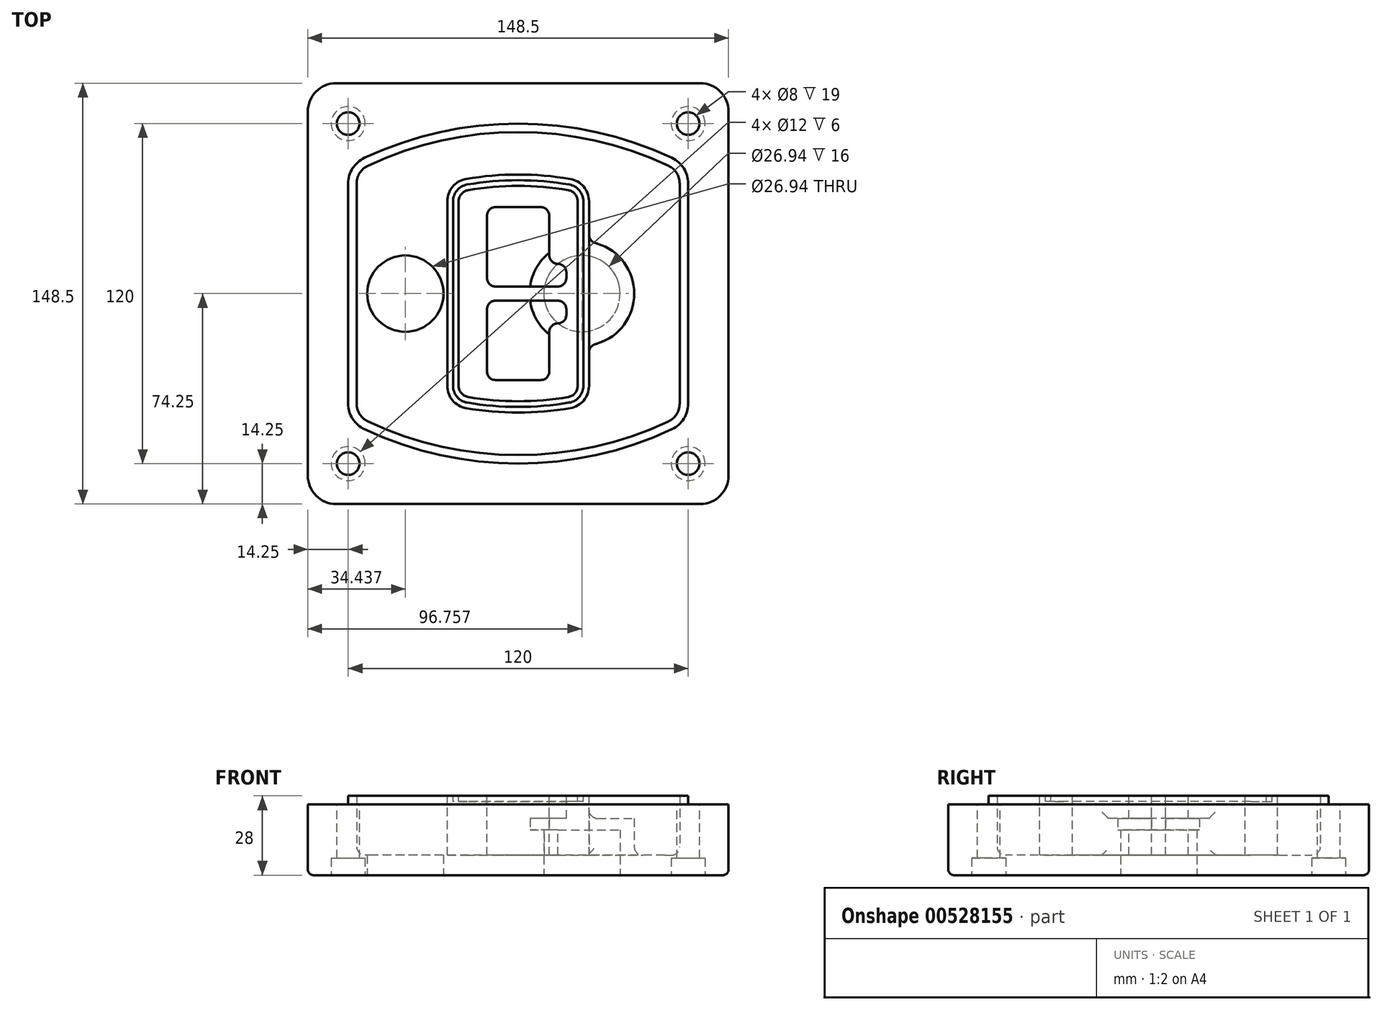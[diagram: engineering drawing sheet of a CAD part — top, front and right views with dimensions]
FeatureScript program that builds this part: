
annotation { "Feature Type Name" : "Feature", "Feature Type Description" : "" }
export const myFeature = defineFeature(function(context is Context, id is Id, definition is map)
    precondition{}
    {
        {
            var Q0;
            Q0=qCreatedBy(makeId("Top.planeOp"),FACE);
            var sketch = newSketch(context, id + "F0", { "sketchPlane" : qUnion([Q0])});
            skPoint(sketch, "E0.rect.middle", {"position": v(0, 0) * mm});
            skLineSegment(sketch, "E1.bottom", {"start": v(-64.25, -74.25) * mm, "end": v(64.25, -74.25) * mm});
            skLineSegment(sketch, "E1.top", {"start": v(-64.25, 74.25) * mm, "end": v(64.25, 74.25) * mm});
            skLineSegment(sketch, "E1.left", {"start": v(-74.25, -64.25) * mm, "end": v(-74.25, 64.25) * mm});
            skLineSegment(sketch, "E1.right", {"start": v(74.25, -64.25) * mm, "end": v(74.25, 64.25) * mm});
            skLineSegment(sketch, "E2", {"start": v(-74.25, 74.25) * mm, "end": v(74.25, -74.25) * mm, "construction": true});
            skLineSegment(sketch, "E3", {"start": v(74.25, 74.25) * mm, "end": v(-74.25, -74.25) * mm, "construction": true});
            skCircle(sketch, "E4", {"center": v(-60, 60) * mm, "radius": 4 * mm});
            skCircle(sketch, "E5", {"center": v(60, 60) * mm, "radius": 4 * mm});
            skCircle(sketch, "E6", {"center": v(60, -60) * mm, "radius": 4 * mm});
            skCircle(sketch, "E7", {"center": v(-60, -60) * mm, "radius": 4 * mm});
            skLineSegment(sketch, "E8", {"start": v(-60, 60) * mm, "end": v(60, 60) * mm, "construction": true});
            skLineSegment(sketch, "E9", {"start": v(60, 60) * mm, "end": v(60, -60) * mm, "construction": true});
            skLineSegment(sketch, "E10", {"start": v(60, -60) * mm, "end": v(-60, -60) * mm, "construction": true});
            skLineSegment(sketch, "E11", {"start": v(-60, -60) * mm, "end": v(-60, 60) * mm, "construction": true});
            skLineSegment(sketch, "E12", {"start": v(-60, 38.83) * mm, "end": v(-60, -38.83) * mm});
            skLineSegment(sketch, "E13", {"start": v(60, 38.83) * mm, "end": v(60, -38.83) * mm});
            skArc(sketch, "E14", {"start": v(54.26, 47.88) * mm, "mid": v(0, 60) * mm, "end": v(-54.26, 47.88) * mm});
            skArc(sketch, "E15", {"start": v(-54.26, -47.88) * mm, "mid": v(0, -60) * mm, "end": v(54.26, -47.88) * mm});
            skLineSegment(sketch, "E16", {"start": v(-60, 0) * mm, "end": v(60, 0) * mm, "construction": true});
            skPoint(sketch, "E17.visualSharp", {"position": v(-60, -45) * mm});
            skArc(sketch, "E17.filletArc", {"start": v(-60, -38.83) * mm, "mid": v(-58.44, -44.2) * mm, "end": v(-54.26, -47.88) * mm});
            skPoint(sketch, "E18.visualSharp", {"position": v(-60, 45) * mm});
            skArc(sketch, "E18.filletArc", {"start": v(-54.26, 47.88) * mm, "mid": v(-58.44, 44.2) * mm, "end": v(-60, 38.83) * mm});
            skPoint(sketch, "E19.visualSharp", {"position": v(60, 45) * mm});
            skArc(sketch, "E19.filletArc", {"start": v(60, 38.83) * mm, "mid": v(58.44, 44.2) * mm, "end": v(54.26, 47.88) * mm});
            skPoint(sketch, "E20.visualSharp", {"position": v(60, -45) * mm});
            skArc(sketch, "E20.filletArc", {"start": v(54.26, -47.88) * mm, "mid": v(58.44, -44.2) * mm, "end": v(60, -38.83) * mm});
            skPoint(sketch, "E21.visualSharp", {"position": v(-74.25, 74.25) * mm});
            skArc(sketch, "E21.filletArc", {"start": v(-64.25, 74.25) * mm, "mid": v(-71.32, 71.32) * mm, "end": v(-74.25, 64.25) * mm});
            skPoint(sketch, "E22.visualSharp", {"position": v(74.25, 74.25) * mm});
            skArc(sketch, "E22.filletArc", {"start": v(74.25, 64.25) * mm, "mid": v(71.32, 71.32) * mm, "end": v(64.25, 74.25) * mm});
            skPoint(sketch, "E23.visualSharp", {"position": v(74.25, -74.25) * mm});
            skArc(sketch, "E23.filletArc", {"start": v(64.25, -74.25) * mm, "mid": v(71.32, -71.32) * mm, "end": v(74.25, -64.25) * mm});
            skPoint(sketch, "E24.visualSharp", {"position": v(-74.25, -74.25) * mm});
            skArc(sketch, "E24.filletArc", {"start": v(-74.25, -64.25) * mm, "mid": v(-71.32, -71.32) * mm, "end": v(-64.25, -74.25) * mm});
            skArc(sketch, "E25.0", {"start": v(57, 38.83) * mm, "mid": v(55.9, 42.58) * mm, "end": v(52.98, 45.17) * mm});
            skLineSegment(sketch, "E25.1", {"start": v(57, 38.83) * mm, "end": v(57, -38.83) * mm});
            skArc(sketch, "E25.2", {"start": v(52.98, -45.17) * mm, "mid": v(55.9, -42.58) * mm, "end": v(57, -38.83) * mm});
            skArc(sketch, "E25.3", {"start": v(-52.98, -45.17) * mm, "mid": v(0, -57) * mm, "end": v(52.98, -45.17) * mm});
            skArc(sketch, "E25.4", {"start": v(-57, -38.83) * mm, "mid": v(-55.9, -42.58) * mm, "end": v(-52.98, -45.17) * mm});
            skArc(sketch, "E25.5", {"start": v(52.98, 45.17) * mm, "mid": v(0, 57) * mm, "end": v(-52.98, 45.17) * mm});
            skLineSegment(sketch, "E25.6", {"start": v(-57, 38.83) * mm, "end": v(-57, -38.83) * mm});
            skArc(sketch, "E25.7", {"start": v(-52.98, 45.17) * mm, "mid": v(-55.9, 42.58) * mm, "end": v(-57, 38.83) * mm});
            skArc(sketch, "E26.0", {"start": v(-55.96, 51.5) * mm, "mid": v(-61.82, 46.33) * mm, "end": v(-64, 38.83) * mm});
            skArc(sketch, "E26.1", {"start": v(55.96, 51.5) * mm, "mid": v(0, 64) * mm, "end": v(-55.96, 51.5) * mm});
            skArc(sketch, "E26.2", {"start": v(64, 38.83) * mm, "mid": v(61.82, 46.33) * mm, "end": v(55.96, 51.5) * mm});
            skLineSegment(sketch, "E26.3", {"start": v(64, 38.83) * mm, "end": v(64, -38.83) * mm});
            skArc(sketch, "E26.4", {"start": v(55.96, -51.5) * mm, "mid": v(61.82, -46.33) * mm, "end": v(64, -38.83) * mm});
            skLineSegment(sketch, "E26.5", {"start": v(-64, 38.83) * mm, "end": v(-64, -38.83) * mm});
            skArc(sketch, "E26.6", {"start": v(-55.96, -51.5) * mm, "mid": v(0, -64) * mm, "end": v(55.96, -51.5) * mm});
            skArc(sketch, "E26.7", {"start": v(-64, -38.83) * mm, "mid": v(-61.82, -46.33) * mm, "end": v(-55.96, -51.5) * mm});
            skSolve(sketch);
        }
        {
            var Q0;
            Q0=makeQuery(id+"F0.imprint","IMPRINT",FACE,{"disambiguationData":[TD([[makeQuery(id+"F0.imprint","IMPRINT",EDGE,{"derivedFrom":sQuery(id+"F0.wireOp",EDGE,"E1.bottom")}),1.0]])]});
            var Q1;
            Q1=makeQuery(id+"F0.imprint","IMPRINT",FACE,{"disambiguationData":[TD([[makeQuery(id+"F0.imprint","IMPRINT",EDGE,{"derivedFrom":sQuery(id+"F0.wireOp",EDGE,"E12")}),1.0]])]});
            var Q2;
            Q2=makeQuery(id+"F0.imprint","IMPRINT",FACE,{"disambiguationData":[TD([[makeQuery(id+"F0.imprint","IMPRINT",EDGE,{"derivedFrom":sQuery(id+"F0.wireOp",EDGE,"E25.0")}),1.0]])]});
            var Q3;
            Q3=makeQuery(id+"F0.imprint","IMPRINT",FACE,{"disambiguationData":[TD([[makeQuery(id+"F0.imprint","IMPRINT",EDGE,{"derivedFrom":sQuery(id+"F0.wireOp",EDGE,"E12")}),-1.0]])]});
            extrude(context, id + "F1", {"entities" : qUnion([Q0, Q1, Q2, Q3]), "oppositeDirection" : true, "depth" : 25 * mm});
        }
        {
            var Q0;
            Q0=makeQuery(id+"F0.imprint","IMPRINT",FACE,{"disambiguationData":[TD([[makeQuery(id+"F0.imprint","IMPRINT",EDGE,{"derivedFrom":sQuery(id+"F0.wireOp",EDGE,"E12")}),1.0]])]});
            extrude(context, id + "F2", {"entities" : qUnion([Q0]), "operationType" : NewBodyOperationType.ADD, "depth" : 3 * mm});
        }
        {
            var Q0;
            Q0=makeQuery(id+"F0.imprint","IMPRINT",FACE,{"disambiguationData":[TD([[makeQuery(id+"F0.imprint","IMPRINT",EDGE,{"derivedFrom":sQuery(id+"F0.wireOp",EDGE,"E25.0")}),1.0]])]});
            extrude(context, id + "F3", {"entities" : qUnion([Q0]), "operationType" : NewBodyOperationType.REMOVE, "oppositeDirection" : true, "depth" : 18 * mm});
        }
        {
            var Q0;
            Q0=makeQuery(id+"F2.opExtrude","CAP_FACE",FACE,{"disambiguationData":[OSD([sQuery(id+"F0.wireOp",EDGE,"E12"),sQuery(id+"F0.wireOp",EDGE,"E13"),sQuery(id+"F0.wireOp",EDGE,"E14"),sQuery(id+"F0.wireOp",EDGE,"E15"),sQuery(id+"F0.wireOp",EDGE,"E17.filletArc"),sQuery(id+"F0.wireOp",EDGE,"E18.filletArc"),sQuery(id+"F0.wireOp",EDGE,"E19.filletArc"),sQuery(id+"F0.wireOp",EDGE,"E20.filletArc"),sQuery(id+"F0.wireOp",EDGE,"E25.0"),sQuery(id+"F0.wireOp",EDGE,"E25.1"),sQuery(id+"F0.wireOp",EDGE,"E25.2"),sQuery(id+"F0.wireOp",EDGE,"E25.3"),sQuery(id+"F0.wireOp",EDGE,"E25.4"),sQuery(id+"F0.wireOp",EDGE,"E25.5"),sQuery(id+"F0.wireOp",EDGE,"E25.6"),sQuery(id+"F0.wireOp",EDGE,"E25.7")])],"isStart":false});
            var sketch = newSketch(context, id + "F4", { "sketchPlane" : qUnion([Q0])});
            skArc(sketch, "E27.0", {"start": v(-18.34, -40.45) * mm, "mid": v(0, -42) * mm, "end": v(18.34, -40.45) * mm});
            skArc(sketch, "E28.0", {"start": v(18.34, 40.45) * mm, "mid": v(0, 42) * mm, "end": v(-18.34, 40.45) * mm});
            skLineSegment(sketch, "E29", {"start": v(-25, 32.57) * mm, "end": v(-25, -32.57) * mm});
            skLineSegment(sketch, "E30", {"start": v(25, 32.57) * mm, "end": v(25, -32.57) * mm});
            skLineSegment(sketch, "E31", {"start": v(-25, 39.1) * mm, "end": v(25, 39.1) * mm, "construction": true});
            skLineSegment(sketch, "E32", {"start": v(-25, -39.1) * mm, "end": v(25, -39.1) * mm, "construction": true});
            skPoint(sketch, "E33.visualSharp", {"position": v(-25, 39.1) * mm});
            skArc(sketch, "E33.filletArc", {"start": v(-18.34, 40.45) * mm, "mid": v(-23.11, 37.73) * mm, "end": v(-25, 32.57) * mm});
            skPoint(sketch, "E34.visualSharp", {"position": v(25, 39.1) * mm});
            skArc(sketch, "E34.filletArc", {"start": v(25, 32.57) * mm, "mid": v(23.11, 37.73) * mm, "end": v(18.34, 40.45) * mm});
            skPoint(sketch, "E35.visualSharp", {"position": v(25, -39.1) * mm});
            skArc(sketch, "E35.filletArc", {"start": v(18.34, -40.45) * mm, "mid": v(23.11, -37.73) * mm, "end": v(25, -32.57) * mm});
            skPoint(sketch, "E36.visualSharp", {"position": v(-25, -39.1) * mm});
            skArc(sketch, "E36.filletArc", {"start": v(-25, -32.57) * mm, "mid": v(-23.11, -37.73) * mm, "end": v(-18.34, -40.45) * mm});
            skArc(sketch, "E37.0", {"start": v(52.98, 45.17) * mm, "mid": v(0, 57) * mm, "end": v(-52.98, 45.17) * mm});
            skArc(sketch, "E37.1", {"start": v(-52.98, 45.17) * mm, "mid": v(-55.9, 42.58) * mm, "end": v(-57, 38.83) * mm});
            skLineSegment(sketch, "E37.2", {"start": v(-57, 38.83) * mm, "end": v(-57, -38.83) * mm});
            skArc(sketch, "E37.3", {"start": v(-57, -38.83) * mm, "mid": v(-55.9, -42.58) * mm, "end": v(-52.98, -45.17) * mm});
            skArc(sketch, "E37.4", {"start": v(-52.98, -45.17) * mm, "mid": v(0, -57) * mm, "end": v(52.98, -45.17) * mm});
            skArc(sketch, "E37.5", {"start": v(52.98, -45.17) * mm, "mid": v(55.9, -42.58) * mm, "end": v(57, -38.83) * mm});
            skLineSegment(sketch, "E37.6", {"start": v(57, 38.83) * mm, "end": v(57, -38.83) * mm});
            skArc(sketch, "E37.7", {"start": v(57, 38.83) * mm, "mid": v(55.9, 42.58) * mm, "end": v(52.98, 45.17) * mm});
            skLineSegment(sketch, "E38.0", {"start": v(23, 32.57) * mm, "end": v(23, -32.57) * mm});
            skArc(sketch, "E38.1", {"start": v(18, -38.48) * mm, "mid": v(21.58, -36.44) * mm, "end": v(23, -32.57) * mm});
            skArc(sketch, "E38.2", {"start": v(-18, -38.48) * mm, "mid": v(0, -40) * mm, "end": v(18, -38.48) * mm});
            skArc(sketch, "E38.3", {"start": v(-23, -32.57) * mm, "mid": v(-21.58, -36.44) * mm, "end": v(-18, -38.48) * mm});
            skLineSegment(sketch, "E38.4", {"start": v(-23, 32.57) * mm, "end": v(-23, -32.57) * mm});
            skArc(sketch, "E38.5", {"start": v(23, 32.57) * mm, "mid": v(21.58, 36.44) * mm, "end": v(18, 38.48) * mm});
            skArc(sketch, "E38.6", {"start": v(-18, 38.48) * mm, "mid": v(-21.58, 36.44) * mm, "end": v(-23, 32.57) * mm});
            skArc(sketch, "E38.7", {"start": v(18, 38.48) * mm, "mid": v(0, 40) * mm, "end": v(-18, 38.48) * mm});
            skArc(sketch, "E39.0", {"start": v(21, 32.57) * mm, "mid": v(20.06, 35.15) * mm, "end": v(17.67, 36.5) * mm});
            skLineSegment(sketch, "E39.1", {"start": v(21, 32.57) * mm, "end": v(21, -32.57) * mm});
            skArc(sketch, "E39.2", {"start": v(17.67, -36.5) * mm, "mid": v(20.06, -35.15) * mm, "end": v(21, -32.57) * mm});
            skArc(sketch, "E39.3", {"start": v(-17.67, -36.5) * mm, "mid": v(0, -38) * mm, "end": v(17.67, -36.5) * mm});
            skArc(sketch, "E39.4", {"start": v(-21, -32.57) * mm, "mid": v(-20.06, -35.15) * mm, "end": v(-17.67, -36.5) * mm});
            skArc(sketch, "E39.5", {"start": v(17.67, 36.5) * mm, "mid": v(0, 38) * mm, "end": v(-17.67, 36.5) * mm});
            skLineSegment(sketch, "E39.6", {"start": v(-21, 32.57) * mm, "end": v(-21, -32.57) * mm});
            skArc(sketch, "E39.7", {"start": v(-17.67, 36.5) * mm, "mid": v(-20.06, 35.15) * mm, "end": v(-21, 32.57) * mm});
            skLineSegment(sketch, "E40", {"start": v(-25, 0) * mm, "end": v(25, 0) * mm, "construction": true});
            skLineSegment(sketch, "E41", {"start": v(-11, 5.5) * mm, "end": v(-11, 27.5) * mm});
            skLineSegment(sketch, "E42", {"start": v(-8, 30.5) * mm, "end": v(8, 30.5) * mm});
            skLineSegment(sketch, "E43", {"start": v(11, 27.5) * mm, "end": v(11, 13.5) * mm});
            skLineSegment(sketch, "E44", {"start": v(14, 10.5) * mm, "end": v(14, 10.5) * mm});
            skLineSegment(sketch, "E45", {"start": v(17, 7.5) * mm, "end": v(17, 5.5) * mm});
            skLineSegment(sketch, "E46", {"start": v(14, 2.5) * mm, "end": v(-8, 2.5) * mm});
            skPoint(sketch, "E47.visualSharp", {"position": v(-11, 30.5) * mm});
            skArc(sketch, "E47.filletArc", {"start": v(-8, 30.5) * mm, "mid": v(-10.12, 29.62) * mm, "end": v(-11, 27.5) * mm});
            skPoint(sketch, "E48.visualSharp", {"position": v(11, 30.5) * mm});
            skArc(sketch, "E48.filletArc", {"start": v(11, 27.5) * mm, "mid": v(10.12, 29.62) * mm, "end": v(8, 30.5) * mm});
            skPoint(sketch, "E49.visualSharp", {"position": v(11, 10.5) * mm});
            skArc(sketch, "E49.filletArc", {"start": v(11, 13.5) * mm, "mid": v(11.88, 11.38) * mm, "end": v(14, 10.5) * mm});
            skPoint(sketch, "E50.visualSharp", {"position": v(17, 10.5) * mm});
            skArc(sketch, "E50.filletArc", {"start": v(17, 7.5) * mm, "mid": v(16.12, 9.62) * mm, "end": v(14, 10.5) * mm});
            skPoint(sketch, "E51.visualSharp", {"position": v(17, 2.5) * mm});
            skArc(sketch, "E51.filletArc", {"start": v(14, 2.5) * mm, "mid": v(16.12, 3.38) * mm, "end": v(17, 5.5) * mm});
            skPoint(sketch, "E52.visualSharp", {"position": v(-11, 2.5) * mm});
            skArc(sketch, "E52.filletArc", {"start": v(-11, 5.5) * mm, "mid": v(-10.12, 3.38) * mm, "end": v(-8, 2.5) * mm});
            skLineSegment(sketch, "E53.0.MirrorCS", {"start": v(14, -2.5) * mm, "end": v(-8, -2.5) * mm});
            skArc(sketch, "E54.0.MirrorCS", {"start": v(-11, -5.5) * mm, "mid": v(-10.12, -3.38) * mm, "end": v(-8, -2.5) * mm});
            skLineSegment(sketch, "E55.0.MirrorCS", {"start": v(-11, -5.5) * mm, "end": v(-11, -27.5) * mm});
            skArc(sketch, "E56.0.MirrorCS", {"start": v(-8, -30.5) * mm, "mid": v(-10.12, -29.62) * mm, "end": v(-11, -27.5) * mm});
            skLineSegment(sketch, "E57.0.MirrorCS", {"start": v(-8, -30.5) * mm, "end": v(8, -30.5) * mm});
            skArc(sketch, "E58.0.MirrorCS", {"start": v(11, -27.5) * mm, "mid": v(10.12, -29.62) * mm, "end": v(8, -30.5) * mm});
            skLineSegment(sketch, "E59.0.MirrorCS", {"start": v(11, -27.5) * mm, "end": v(11, -13.5) * mm});
            skArc(sketch, "E60.0.MirrorCS", {"start": v(11, -13.5) * mm, "mid": v(11.88, -11.38) * mm, "end": v(14, -10.5) * mm});
            skArc(sketch, "E61.0.MirrorCS", {"start": v(17, -7.5) * mm, "mid": v(16.12, -9.62) * mm, "end": v(14, -10.5) * mm});
            skLineSegment(sketch, "E62.0.MirrorCS", {"start": v(17, -7.5) * mm, "end": v(17, -5.5) * mm});
            skArc(sketch, "E63.0.MirrorCS", {"start": v(14, -2.5) * mm, "mid": v(16.12, -3.38) * mm, "end": v(17, -5.5) * mm});
            skSolve(sketch);
        }
        {
            var Q0;
            Q0=makeQuery(id+"F4.imprint","IMPRINT",FACE,{"disambiguationData":[TD([[makeQuery(id+"F4.imprint","IMPRINT",EDGE,{"derivedFrom":sQuery(id+"F4.wireOp",EDGE,"E27.0")}),1.0]])]});
            var Q1;
            Q1=makeQuery(id+"F4.imprint","IMPRINT",FACE,{"disambiguationData":[TD([[makeQuery(id+"F4.imprint","IMPRINT",EDGE,{"derivedFrom":sQuery(id+"F4.wireOp",EDGE,"E38.0")}),-1.0]])]});
            var Q2;
            Q2=makeQuery(id+"F4.imprint","IMPRINT",FACE,{"disambiguationData":[TD([[makeQuery(id+"F4.imprint","IMPRINT",EDGE,{"derivedFrom":sQuery(id+"F4.wireOp",EDGE,"E39.0")}),1.0]])]});
            extrude(context, id + "F5", {"entities" : qUnion([Q0, Q1, Q2]), "operationType" : NewBodyOperationType.ADD, "endBound" : BoundingType.UP_TO_NEXT, "oppositeDirection" : true, "depth" : 25 * mm});
        }
        {
            var Q0;
            Q0=makeQuery(id+"F4.imprint","IMPRINT",FACE,{"disambiguationData":[TD([[makeQuery(id+"F4.imprint","IMPRINT",EDGE,{"derivedFrom":sQuery(id+"F4.wireOp",EDGE,"E38.0")}),-1.0]])]});
            extrude(context, id + "F6", {"entities" : qUnion([Q0]), "operationType" : NewBodyOperationType.REMOVE, "oppositeDirection" : true, "depth" : 2 * mm});
        }
        {
            var Q0;
            Q0=makeQuery(id+"F1.opExtrude","CAP_FACE",FACE,{"disambiguationData":[OSD([sQuery(id+"F0.wireOp",EDGE,"E1.bottom"),sQuery(id+"F0.wireOp",EDGE,"E1.top"),sQuery(id+"F0.wireOp",EDGE,"E1.left"),sQuery(id+"F0.wireOp",EDGE,"E1.right"),sQuery(id+"F0.wireOp",EDGE,"E4"),sQuery(id+"F0.wireOp",EDGE,"E5"),sQuery(id+"F0.wireOp",EDGE,"E6"),sQuery(id+"F0.wireOp",EDGE,"E7"),sQuery(id+"F0.wireOp",EDGE,"E21.filletArc"),sQuery(id+"F0.wireOp",EDGE,"E22.filletArc"),sQuery(id+"F0.wireOp",EDGE,"E23.filletArc"),sQuery(id+"F0.wireOp",EDGE,"E24.filletArc")])],"isStart":false});
            var sketch = newSketch(context, id + "F7", { "sketchPlane" : qUnion([Q0])});
            skCircle(sketch, "E64", {"center": v(22.5, 0) * mm, "radius": 13.47 * mm});
            skCircle(sketch, "E65", {"center": v(-39.81, 0) * mm, "radius": 13.47 * mm});
            skLineSegment(sketch, "E66", {"start": v(74.25, 0) * mm, "end": v(-74.25, 0) * mm});
            skCircle(sketch, "E67", {"center": v(22.5, 0) * mm, "radius": 18.47 * mm});
            skCircle(sketch, "E68", {"center": v(60, -60) * mm, "radius": 6 * mm});
            skCircle(sketch, "E69", {"center": v(-60, -60) * mm, "radius": 6 * mm});
            skCircle(sketch, "E70", {"center": v(-60, 60) * mm, "radius": 6 * mm});
            skCircle(sketch, "E71", {"center": v(60, 60) * mm, "radius": 6 * mm});
            skSolve(sketch);
        }
        {
            var Q0;
            {var subQ1=sQuery(id+"F7.wireOp",EDGE,"E66");var subQ4=sQuery(id+"F7.wireOp",EDGE,"E64");var subQ6=makeQuery(id+"F7.imprint","INTERSECT",VERTEX,{"disambiguationData":[OD(0.0)],"derivedFrom":[subQ4,subQ1]});Q0=makeQuery(id+"F7.imprint","IMPRINT",FACE,{"disambiguationData":[TD([[makeQuery(id+"F7.imprint","IMPRINT",EDGE,{"disambiguationData":[TD([[subQ6,-1.0]])],"derivedFrom":subQ4}),-1.0]])]});}
            var Q1;
            {var subQ0=sQuery(id+"F7.wireOp",EDGE,"E66");var subQ1=sQuery(id+"F7.wireOp",EDGE,"E64");var subQ3=makeQuery(id+"F7.imprint","INTERSECT",VERTEX,{"disambiguationData":[OD(0.0)],"derivedFrom":[subQ1,subQ0]});Q1=makeQuery(id+"F7.imprint","IMPRINT",FACE,{"disambiguationData":[TD([[makeQuery(id+"F7.imprint","IMPRINT",EDGE,{"disambiguationData":[TD([[subQ3,-1.0]])],"derivedFrom":subQ1}),1.0]])]});}
            var Q2;
            {var subQ0=sQuery(id+"F7.wireOp",EDGE,"E66");var subQ1=sQuery(id+"F7.wireOp",EDGE,"E64");var subQ3=makeQuery(id+"F7.imprint","INTERSECT",VERTEX,{"disambiguationData":[OD(0.0)],"derivedFrom":[subQ1,subQ0]});Q2=makeQuery(id+"F7.imprint","IMPRINT",FACE,{"disambiguationData":[TD([[makeQuery(id+"F7.imprint","IMPRINT",EDGE,{"disambiguationData":[TD([[subQ3,1.0]])],"derivedFrom":subQ1}),1.0]])]});}
            var Q3;
            {var subQ1=sQuery(id+"F7.wireOp",EDGE,"E66");var subQ4=sQuery(id+"F7.wireOp",EDGE,"E64");var subQ6=makeQuery(id+"F7.imprint","INTERSECT",VERTEX,{"disambiguationData":[OD(0.0)],"derivedFrom":[subQ4,subQ1]});Q3=makeQuery(id+"F7.imprint","IMPRINT",FACE,{"disambiguationData":[TD([[makeQuery(id+"F7.imprint","IMPRINT",EDGE,{"disambiguationData":[TD([[subQ6,1.0]])],"derivedFrom":subQ4}),-1.0]])]});}
            extrude(context, id + "F8", {"entities" : qUnion([Q0, Q1, Q2, Q3]), "operationType" : NewBodyOperationType.ADD, "oppositeDirection" : true, "depth" : 20 * mm});
        }
        {
            var Q0;
            {var subQ0=sQuery(id+"F7.wireOp",EDGE,"E66");var subQ1=sQuery(id+"F7.wireOp",EDGE,"E64");var subQ3=makeQuery(id+"F7.imprint","INTERSECT",VERTEX,{"disambiguationData":[OD(0.0)],"derivedFrom":[subQ1,subQ0]});Q0=makeQuery(id+"F7.imprint","IMPRINT",FACE,{"disambiguationData":[TD([[makeQuery(id+"F7.imprint","IMPRINT",EDGE,{"disambiguationData":[TD([[subQ3,-1.0]])],"derivedFrom":subQ1}),1.0]])]});}
            var Q1;
            {var subQ0=sQuery(id+"F7.wireOp",EDGE,"E66");var subQ1=sQuery(id+"F7.wireOp",EDGE,"E64");var subQ3=makeQuery(id+"F7.imprint","INTERSECT",VERTEX,{"disambiguationData":[OD(0.0)],"derivedFrom":[subQ1,subQ0]});Q1=makeQuery(id+"F7.imprint","IMPRINT",FACE,{"disambiguationData":[TD([[makeQuery(id+"F7.imprint","IMPRINT",EDGE,{"disambiguationData":[TD([[subQ3,1.0]])],"derivedFrom":subQ1}),1.0]])]});}
            extrude(context, id + "F9", {"entities" : qUnion([Q0, Q1]), "operationType" : NewBodyOperationType.REMOVE, "oppositeDirection" : true, "depth" : 16 * mm});
        }
        {
            var Q0;
            {var subQ0=sQuery(id+"F7.wireOp",EDGE,"E66");var subQ1=sQuery(id+"F7.wireOp",EDGE,"E65");var subQ3=makeQuery(id+"F7.imprint","INTERSECT",VERTEX,{"disambiguationData":[OD(0.0)],"derivedFrom":[subQ1,subQ0]});Q0=makeQuery(id+"F7.imprint","IMPRINT",FACE,{"disambiguationData":[TD([[makeQuery(id+"F7.imprint","IMPRINT",EDGE,{"disambiguationData":[TD([[subQ3,-1.0]])],"derivedFrom":subQ1}),1.0]])]});}
            var Q1;
            {var subQ0=sQuery(id+"F7.wireOp",EDGE,"E66");var subQ1=sQuery(id+"F7.wireOp",EDGE,"E65");var subQ3=makeQuery(id+"F7.imprint","INTERSECT",VERTEX,{"disambiguationData":[OD(0.0)],"derivedFrom":[subQ1,subQ0]});Q1=makeQuery(id+"F7.imprint","IMPRINT",FACE,{"disambiguationData":[TD([[makeQuery(id+"F7.imprint","IMPRINT",EDGE,{"disambiguationData":[TD([[subQ3,1.0]])],"derivedFrom":subQ1}),1.0]])]});}
            extrude(context, id + "F10", {"entities" : qUnion([Q0, Q1]), "operationType" : NewBodyOperationType.REMOVE, "oppositeDirection" : true, "depth" : 25 * mm});
        }
        {
            var Q0;
            Q0=makeQuery(id+"F7.imprint","IMPRINT",FACE,{"disambiguationData":[TD([[makeQuery(id+"F7.imprint","IMPRINT",EDGE,{"derivedFrom":sQuery(id+"F7.wireOp",EDGE,"E68")}),1.0]])]});
            var Q1;
            Q1=makeQuery(id+"F7.imprint","IMPRINT",FACE,{"disambiguationData":[TD([[makeQuery(id+"F7.imprint","IMPRINT",EDGE,{"derivedFrom":makeQuery(id+"F1.opExtrude","CAP_EDGE",EDGE,{"disambiguationData":[OSD([sQuery(id+"F0.wireOp",EDGE,"E5")])],"isStart":false})}),-1.0]])]});
            var Q2;
            Q2=makeQuery(id+"F7.imprint","IMPRINT",FACE,{"disambiguationData":[TD([[makeQuery(id+"F7.imprint","IMPRINT",EDGE,{"derivedFrom":sQuery(id+"F7.wireOp",EDGE,"E69")}),1.0]])]});
            var Q3;
            Q3=makeQuery(id+"F7.imprint","IMPRINT",FACE,{"disambiguationData":[TD([[makeQuery(id+"F7.imprint","IMPRINT",EDGE,{"derivedFrom":makeQuery(id+"F1.opExtrude","CAP_EDGE",EDGE,{"disambiguationData":[OSD([sQuery(id+"F0.wireOp",EDGE,"E4")])],"isStart":false})}),-1.0]])]});
            var Q4;
            Q4=makeQuery(id+"F7.imprint","IMPRINT",FACE,{"disambiguationData":[TD([[makeQuery(id+"F7.imprint","IMPRINT",EDGE,{"derivedFrom":sQuery(id+"F7.wireOp",EDGE,"E70")}),1.0]])]});
            var Q5;
            Q5=makeQuery(id+"F7.imprint","IMPRINT",FACE,{"disambiguationData":[TD([[makeQuery(id+"F7.imprint","IMPRINT",EDGE,{"derivedFrom":makeQuery(id+"F1.opExtrude","CAP_EDGE",EDGE,{"disambiguationData":[OSD([sQuery(id+"F0.wireOp",EDGE,"E7")])],"isStart":false})}),-1.0]])]});
            var Q6;
            Q6=makeQuery(id+"F7.imprint","IMPRINT",FACE,{"disambiguationData":[TD([[makeQuery(id+"F7.imprint","IMPRINT",EDGE,{"derivedFrom":sQuery(id+"F7.wireOp",EDGE,"E71")}),1.0]])]});
            var Q7;
            Q7=makeQuery(id+"F7.imprint","IMPRINT",FACE,{"disambiguationData":[TD([[makeQuery(id+"F7.imprint","IMPRINT",EDGE,{"derivedFrom":makeQuery(id+"F1.opExtrude","CAP_EDGE",EDGE,{"disambiguationData":[OSD([sQuery(id+"F0.wireOp",EDGE,"E6")])],"isStart":false})}),-1.0]])]});
            extrude(context, id + "F11", {"entities" : qUnion([Q0, Q1, Q2, Q3, Q4, Q5, Q6, Q7]), "operationType" : NewBodyOperationType.REMOVE, "oppositeDirection" : true, "depth" : 6 * mm});
        }
        {
            var Q0;
            Q0=makeQuery(id+"F9.boolean.opBoolean","COPY",FACE,{"derivedFrom":makeQuery(id+"F9.opExtrude","CAP_FACE",FACE,{"disambiguationData":[OSD([sQuery(id+"F7.wireOp",EDGE,"E64")])],"isStart":false})});
            var sketch = newSketch(context, id + "F12", { "sketchPlane" : qUnion([Q0])});
            skArc(sketch, "E72.0", {"start": v(11, 14.45) * mm, "mid": v(6.45, 9.13) * mm, "end": v(4.2, 2.5) * mm});
            skArc(sketch, "E72.1", {"start": v(4.2, -2.5) * mm, "mid": v(6.45, -9.13) * mm, "end": v(11, -14.45) * mm});
            skLineSegment(sketch, "E73", {"start": v(4.2, -2.5) * mm, "end": v(14, -2.5) * mm});
            skLineSegment(sketch, "E74.0", {"start": v(14, 2.5) * mm, "end": v(4.2, 2.5) * mm});
            skArc(sketch, "E74.1", {"start": v(14, 2.5) * mm, "mid": v(16.12, 3.38) * mm, "end": v(17, 5.5) * mm});
            skLineSegment(sketch, "E74.2", {"start": v(17, 7.5) * mm, "end": v(17, 5.5) * mm});
            skArc(sketch, "E74.3", {"start": v(17, 7.5) * mm, "mid": v(16.12, 9.62) * mm, "end": v(14, 10.5) * mm});
            skArc(sketch, "E74.4", {"start": v(11, 13.5) * mm, "mid": v(11.88, 11.38) * mm, "end": v(14, 10.5) * mm});
            skLineSegment(sketch, "E74.5", {"start": v(11, 14.45) * mm, "end": v(11, 13.5) * mm});
            skLineSegment(sketch, "E74.7", {"start": v(14, -2.5) * mm, "end": v(4.2, -2.5) * mm});
            skArc(sketch, "E74.8", {"start": v(14, -2.5) * mm, "mid": v(16.12, -3.38) * mm, "end": v(17, -5.5) * mm});
            skLineSegment(sketch, "E74.9", {"start": v(17, -7.5) * mm, "end": v(17, -5.5) * mm});
            skArc(sketch, "E74.10", {"start": v(17, -7.5) * mm, "mid": v(16.12, -9.62) * mm, "end": v(14, -10.5) * mm});
            skArc(sketch, "E74.11", {"start": v(11, -13.5) * mm, "mid": v(11.88, -11.38) * mm, "end": v(14, -10.5) * mm});
            skLineSegment(sketch, "E74.12", {"start": v(11, -14.45) * mm, "end": v(11, -13.5) * mm});
            skPoint(sketch, "E75.orphan", {"position": v(11, -27.5) * mm});
            skPoint(sketch, "E76.orphan", {"position": v(-8, -2.5) * mm});
            skPoint(sketch, "E77.orphan", {"position": v(-8, 2.5) * mm});
            skPoint(sketch, "E78.orphan", {"position": v(11, 27.5) * mm});
            skSolve(sketch);
        }
        {
            var Q0;
            {var subQ7=sQuery(id+"F12.wireOp",EDGE,"E72.0");var subQ14=sQuery(id+"F12.wireOp",EDGE,"E72.1");var subQ16=sQuery(id+"F12.wireOp",EDGE,"E74.1");var subQ18=sQuery(id+"F12.wireOp",EDGE,"E74.8");Q0=qUnion([makeQuery(id+"F12.imprint","IMPRINT",FACE,{"disambiguationData":[TD([[makeQuery(id+"F12.imprint","IMPRINT",EDGE,{"derivedFrom":subQ7}),1.0]])]}),makeQuery(id+"F12.imprint","IMPRINT",FACE,{"disambiguationData":[TD([[makeQuery(id+"F12.imprint","IMPRINT",EDGE,{"derivedFrom":subQ14}),1.0]])]}),makeQuery(id+"F12.imprint","IMPRINT",FACE,{"disambiguationData":[TD([[makeQuery(id+"F12.imprint","IMPRINT",EDGE,{"derivedFrom":subQ16}),1.0]])]}),makeQuery(id+"F12.imprint","IMPRINT",FACE,{"disambiguationData":[TD([[makeQuery(id+"F12.imprint","IMPRINT",EDGE,{"derivedFrom":subQ18}),-1.0]])]})]);}
            var Q1;
            Q1=makeQuery(id+"F5.boolean.opBoolean","SPLIT",FACE,{"disambiguationData":[TD([makeQuery(id+"F5.opExtrude","SWEPT_FACE",FACE,{"disambiguationData":[OSD([sQuery(id+"F4.wireOp",EDGE,"E41")])]})])],"derivedFrom":makeQuery(id+"F3.boolean.opBoolean","COPY",FACE,{"derivedFrom":makeQuery(id+"F3.opExtrude","CAP_FACE",FACE,{"disambiguationData":[OSD([sQuery(id+"F0.wireOp",EDGE,"E25.0"),sQuery(id+"F0.wireOp",EDGE,"E25.1"),sQuery(id+"F0.wireOp",EDGE,"E25.2"),sQuery(id+"F0.wireOp",EDGE,"E25.3"),sQuery(id+"F0.wireOp",EDGE,"E25.4"),sQuery(id+"F0.wireOp",EDGE,"E25.5"),sQuery(id+"F0.wireOp",EDGE,"E25.6"),sQuery(id+"F0.wireOp",EDGE,"E25.7")])],"isStart":false})})});
            extrude(context, id + "F13", {"entities" : qUnion([Q0]), "operationType" : NewBodyOperationType.REMOVE, "endBound" : BoundingType.UP_TO_SURFACE, "endBoundEntityFace" : qUnion([Q1]), "depth" : 25 * mm});
        }
        {
            var Q0;
            Q0=makeQuery(id+"F3.boolean.opBoolean","COPY",EDGE,{"derivedFrom":makeQuery(id+"F3.opExtrude","CAP_EDGE",EDGE,{"disambiguationData":[OSD([sQuery(id+"F0.wireOp",EDGE,"E25.6")])],"isStart":false})});
            var Q1;
            Q1=makeQuery(id+"F8.boolean.opBoolean","INTERSECT",EDGE,{"derivedFrom":[makeQuery(id+"F5.opExtrude","SWEPT_FACE",FACE,{"disambiguationData":[OSD([sQuery(id+"F4.wireOp",EDGE,"E30")])]}),makeQuery(id+"F8.opExtrude","CAP_FACE",FACE,{"disambiguationData":[OSD([sQuery(id+"F7.wireOp",EDGE,"E67")])],"isStart":false})]});
            var Q2;
            Q2=makeQuery(id+"F8.boolean.opBoolean","INTERSECT",EDGE,{"disambiguationData":[OD(1.0)],"derivedFrom":[makeQuery(id+"F5.opExtrude","SWEPT_FACE",FACE,{"disambiguationData":[OSD([sQuery(id+"F4.wireOp",EDGE,"E30")])]}),makeQuery(id+"F8.opExtrude","SWEPT_FACE",FACE,{"disambiguationData":[OSD([sQuery(id+"F7.wireOp",EDGE,"E67")])]})]});
            var Q3;
            {var subQ0=makeQuery(id+"F3.boolean.opBoolean","COPY",FACE,{"derivedFrom":makeQuery(id+"F3.opExtrude","CAP_FACE",FACE,{"disambiguationData":[OSD([sQuery(id+"F0.wireOp",EDGE,"E25.0"),sQuery(id+"F0.wireOp",EDGE,"E25.1"),sQuery(id+"F0.wireOp",EDGE,"E25.2"),sQuery(id+"F0.wireOp",EDGE,"E25.3"),sQuery(id+"F0.wireOp",EDGE,"E25.4"),sQuery(id+"F0.wireOp",EDGE,"E25.5"),sQuery(id+"F0.wireOp",EDGE,"E25.6"),sQuery(id+"F0.wireOp",EDGE,"E25.7")])],"isStart":false})});var subQ1=sQuery(id+"F4.wireOp",EDGE,"E30");Q3=makeQuery(id+"F8.boolean.opBoolean","SPLIT",EDGE,{"disambiguationData":[TD([makeQuery(id+"F5.opExtrude","SWEPT_FACE",FACE,{"disambiguationData":[OSD([sQuery(id+"F4.wireOp",EDGE,"E35.filletArc")])]})])],"derivedFrom":makeQuery(id+"F5.opExtrude","TWEAK_EDGE",EDGE,{"derivedFrom":[subQ0,makeQuery(id+"F4.imprint","IMPRINT",EDGE,{"derivedFrom":subQ1})]})});}
            var Q4;
            {var subQ0=sQuery(id+"F0.wireOp",EDGE,"E25.0");var subQ1=sQuery(id+"F0.wireOp",EDGE,"E25.1");var subQ2=sQuery(id+"F0.wireOp",EDGE,"E25.2");var subQ3=sQuery(id+"F0.wireOp",EDGE,"E25.3");var subQ4=sQuery(id+"F0.wireOp",EDGE,"E25.4");var subQ5=sQuery(id+"F0.wireOp",EDGE,"E25.5");var subQ6=sQuery(id+"F0.wireOp",EDGE,"E25.6");var subQ7=sQuery(id+"F0.wireOp",EDGE,"E25.7");Q4=makeQuery(id+"F8.boolean.opBoolean","INTERSECT",EDGE,{"derivedFrom":[makeQuery(id+"F5.boolean.opBoolean","SPLIT",FACE,{"disambiguationData":[TD([makeQuery(id+"F2.opExtrude","SWEPT_FACE",FACE,{"disambiguationData":[OSD([subQ0])]})])],"derivedFrom":makeQuery(id+"F3.boolean.opBoolean","COPY",FACE,{"derivedFrom":makeQuery(id+"F3.opExtrude","CAP_FACE",FACE,{"disambiguationData":[OSD([subQ0,subQ1,subQ2,subQ3,subQ4,subQ5,subQ6,subQ7])],"isStart":false})})}),makeQuery(id+"F8.opExtrude","SWEPT_FACE",FACE,{"disambiguationData":[OSD([sQuery(id+"F7.wireOp",EDGE,"E67")])]})]});}
            var Q5;
            Q5=makeQuery(id+"F8.boolean.opBoolean","INTERSECT",EDGE,{"disambiguationData":[OD(0.0)],"derivedFrom":[makeQuery(id+"F5.opExtrude","SWEPT_FACE",FACE,{"disambiguationData":[OSD([sQuery(id+"F4.wireOp",EDGE,"E30")])]}),makeQuery(id+"F8.opExtrude","SWEPT_FACE",FACE,{"disambiguationData":[OSD([sQuery(id+"F7.wireOp",EDGE,"E67")])]})]});
            fillet(context, id + "F14", {"entities" : qUnion([Q0, Q1, Q2, Q3, Q4, Q5]), "radius" : 3 * mm, "tangentPropagation" : true, "allowEdgeOverflow" : false});
        }
        {
            var Q0;
            Q0=makeQuery(id+"F1.opExtrude","CAP_EDGE",EDGE,{"disambiguationData":[OSD([sQuery(id+"F0.wireOp",EDGE,"E1.bottom")])],"isStart":false});
            fillet(context, id + "F15", {"entities" : qUnion([Q0]), "radius" : 2 * mm, "tangentPropagation" : true, "allowEdgeOverflow" : false});
        }
        {
            var Q0;
            Q0=qCreatedBy(makeId("Top.planeOp"),FACE);
            var sketch = newSketch(context, id + "F16", { "sketchPlane" : qUnion([Q0])});
            skLineSegment(sketch, "E79", {"start": v(-11.57, 92.3) * mm, "end": v(-11.57, 104.29) * mm});
            skLineSegment(sketch, "E80", {"start": v(18.43, 92.27) * mm, "end": v(18.43, 104.29) * mm});
            skArc(sketch, "E81", {"start": v(18.43, 104.29) * mm, "mid": v(3.43, 119.29) * mm, "end": v(-11.57, 104.29) * mm});
            skLineSegment(sketch, "E82", {"start": v(-11.57, 92.3) * mm, "end": v(-35, 74.33) * mm});
            skLineSegment(sketch, "E83", {"start": v(3.43, 104.29) * mm, "end": v(3.43, 74.29) * mm, "construction": true});
            skCircle(sketch, "E84", {"center": v(3.43, 104.29) * mm, "radius": 6 * mm});
            skLineSegment(sketch, "E85", {"start": v(-74.25, 0) * mm, "end": v(74.25, 0) * mm, "construction": true});
            skCircle(sketch, "E86.MirrorC", {"center": v(3.43, -104.29) * mm, "radius": 6 * mm});
            skArc(sketch, "E87.MirrorCS", {"start": v(18.43, -104.29) * mm, "mid": v(3.43, -119.29) * mm, "end": v(-11.57, -104.29) * mm});
            skLineSegment(sketch, "E88.MirrorCS", {"start": v(18.43, -92.27) * mm, "end": v(18.43, -104.29) * mm});
            skLineSegment(sketch, "E89.MirrorCS", {"start": v(-11.57, -92.3) * mm, "end": v(-35, -74.33) * mm});
            skLineSegment(sketch, "E90.MirrorCS", {"start": v(3.43, -104.29) * mm, "end": v(3.43, -74.29) * mm, "construction": true});
            skLineSegment(sketch, "E91.MirrorCS", {"start": v(-11.57, -92.3) * mm, "end": v(-11.57, -104.29) * mm});
            skLineSegment(sketch, "E92", {"start": v(18.43, 92.27) * mm, "end": v(36.41, 74.26) * mm});
            skLineSegment(sketch, "E93", {"start": v(36.41, 74.26) * mm, "end": v(36.42, 74.25) * mm});
            skLineSegment(sketch, "E94", {"start": v(-35.11, 74.32) * mm, "end": v(-35.11, 74.32) * mm});
            skLineSegment(sketch, "E95", {"start": v(36.42, 74.25) * mm, "end": v(36.42, 74.25) * mm});
            skLineSegment(sketch, "E96", {"start": v(36.42, 74.25) * mm, "end": v(-35.13, 74.25) * mm});
            skLineSegment(sketch, "E97", {"start": v(-35.13, 74.25) * mm, "end": v(-35, 74.33) * mm});
            skLineSegment(sketch, "E98", {"start": v(-35, -74.33) * mm, "end": v(-35.1, -74.25) * mm});
            skLineSegment(sketch, "E99", {"start": v(18.43, -92.27) * mm, "end": v(36.41, -74.26) * mm});
            skLineSegment(sketch, "E100", {"start": v(-35.1, -74.25) * mm, "end": v(36.42, -74.25) * mm});
            skLineSegment(sketch, "E101", {"start": v(36.42, -74.25) * mm, "end": v(36.41, -74.26) * mm});
            skSolve(sketch);
        }
    });
